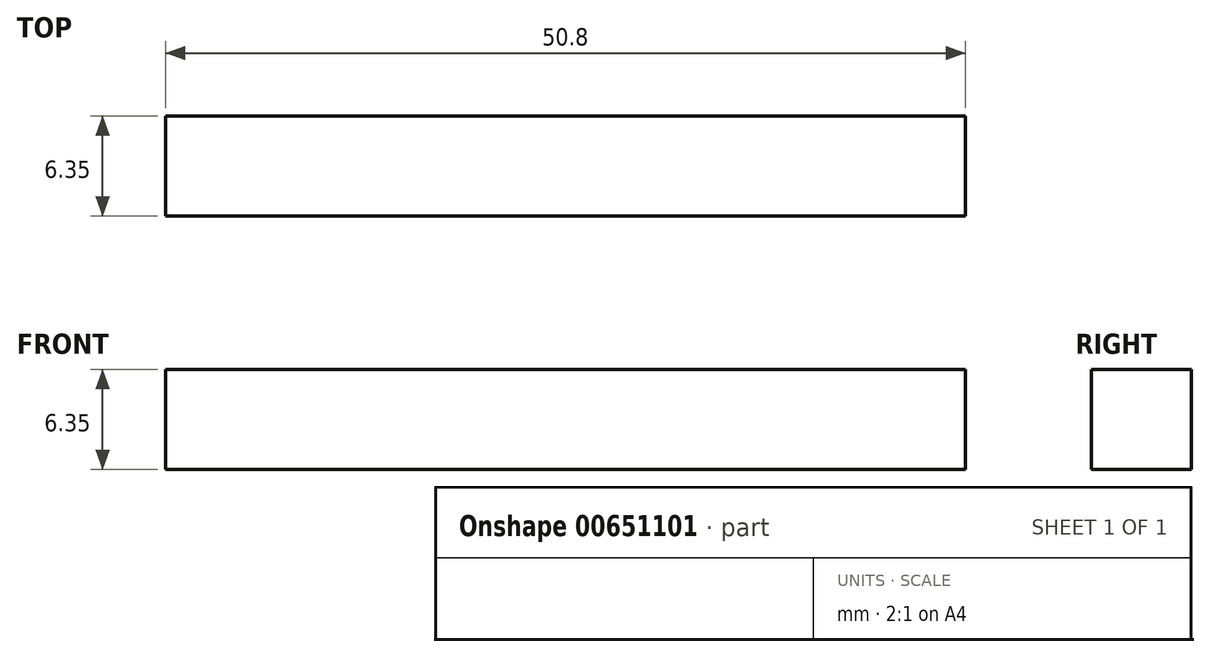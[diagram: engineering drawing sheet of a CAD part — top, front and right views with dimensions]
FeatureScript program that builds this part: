
annotation { "Feature Type Name" : "Feature", "Feature Type Description" : "" }
export const myFeature = defineFeature(function(context is Context, id is Id, definition is map)
    precondition{}
    {
        {
            var Q0;
            Q0=qCreatedBy(makeId("Top.planeOp"),FACE);
            var sketch = newSketch(context, id + "F0", { "sketchPlane" : qUnion([Q0])});
            skLineSegment(sketch, "E0", {"start": v(0, 0) * mm, "end": v(-50.8, 0) * mm});
            skLineSegment(sketch, "E1", {"start": v(-50.8, 0) * mm, "end": v(-50.8, -6.35) * mm});
            skLineSegment(sketch, "E2", {"start": v(-50.8, -6.35) * mm, "end": v(0, -6.35) * mm});
            skLineSegment(sketch, "E3", {"start": v(0, -6.35) * mm, "end": v(0, 0) * mm});
            skSolve(sketch);
        }
        {
            var Q0;
            Q0 = qSketchRegion(id + "F0", true);
            extrude(context, id + "F1", {"entities" : qUnion([Q0]), "depth" : 6.35 * mm, "offsetDistance" : 25.4 * mm});
        }
    });
